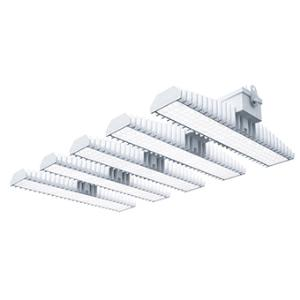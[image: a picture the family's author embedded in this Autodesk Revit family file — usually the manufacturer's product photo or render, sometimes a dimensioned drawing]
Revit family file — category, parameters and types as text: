
# Revit family: 3f_filippi_-_3f_lem_ho_ampio_3f_filippi_-_58976_a0812_-_3f_lem_5_ho_led_350_dali_cr_ampio___vs_a41a
name_source: partatom
category: Lighting Fixtures
units: mm (PartAtom-declared; Revit-internal decimal feet)

## family parameters
Cut with Voids When Loaded = No
Host = Face
Light Source = No
Part Type = Normal
Room Calculation Point = No
Round Connector Dimension = Use Diameter
Shared = No

## types (1)
- 3F Filippi - 3F LEM HO Ampio (1 x LED, 44256 lm, 345 W, 4000 K)
    Apparent Load = 345 VA
    Approval mark = CE
    CIE Flux Codes = 67 90 97 100 100
    Color Rendering = 80
    Color Temperature = 4000 K
    Control Gear = Electronic transformer
    Default Elevation = 1800 mm
    Description = Industrial luminaire with high light output and high luminous efficiency designed with the most innovative technologies for environments with temperature up to 55°C.

ILLUMINOTECHNICAL
Luminous efficiency 100% (DLOR 98%, ULOR 2%).
Initial luminous flux of the luminaire 44256 lm.
Direct symmetric wide distribution: the illuminated area has a rectangular shape.
Installation Interdistance Transv.D = 1.24 x hu - Long.D = 1.20 x hu.
Tabular UGR (CIE 117 - 4H-8H; S=0.25H; 70/50/20): RUG 23.8 - 23.9.
Beam angle: 82° - 83°.
Luminous efficacy 128 lm/W.
Lifetime (L93/B10): 30000 h. (tq+25°C)
Lifetime (L90/B10): 50000 h. (tq+25°C)
Lifetime (L85/B10): 80000 h. (tq+25°C)
Lifetime (L80/B10): 100000 h. (tq+25°C)
Lifetime (L85/B10): 50000 h. (tq+55°C)
Sudden decreased luminous flux after 50000 hours: 0% (C0).
Photobiological safety in compliance with IEC/TR 62778: RG0 risk exempt, (IEC 62471).
In compliance with IEC/EN 62722-2-1 - IEC/EN 62717 standards.

SOURCE
5 Mid-Power linear LED modules 70W/840.
Energy efficiency class (UE 2019/2020 - UE 2019/2015): C.
CIE 13.3 Colour rendering index: CRI >80 (R9 <50%).
IES TM-30 Fidelity Index: Rf = 84 Rg = 95.
CCT nominal colour temperature 4000 K.
Colour initial tolerance (MacAdam): SDCM 3.

MECHANICAL
Passive modular heatsinks in die-casted aluminium, painted in white colour.
To optimize the thermal management of the LED module, the heatsinks are oversized and provided with self-cleaning of cooling fins.
Wiring body in aluminium and galvanised steel anchored solidly to the sinks and thermally separated.
3F Lens lenses with high luminous efficiency, transparent methacrylate (PMMA), fixed to the LED modules.
Fixing brackets in stainless steel.
Luminaire with limited surface temperature. - D - (EN 60598-2-24)
Dimensions: 952x542 mm, height 133 mm. Weight 24.13 kg.
IP65 protection degree.
Mechanical strength to impacts IK06 (1 joule).
Glow-wire test resistance 650°C.

ELECTRICAL
Halogen Free DALI-2 DATI (Parts 251, 252, 253), PUSH-DIM, electronic wiring 230V-50/60Hz, power factor 0.97 at full load, THD <25%, constant output current, class I, 3 driver, 3 DALI addresses.
Power of the luminaire 345 W.
ENEC - CE.
SAFE FLICKER: PstLM=<1 and SVM=<0.4 (IEC TR 61547-1 and IEC TR 63158), to ensure a more comfortable and safe light.
Luminaire compliant with EN 60598-2-22 for power supply from a centralised emergency system CPSS (Central Power Supply System), not incorporated in the luminaire - high risk areas excluded. The default power and flux are 100% in AC and 15% in DC.
Ambient temperature from -30°C to +55°C.
Temperature class T6 max 85°C.
Quick connection via M25 5P connector with 9-13 mm tightening range.
Power unit positioned on a separate compartment by the LED module to ensure optimum temperatures of cabling components, to be inspectable and maintainable.
Relative humidity UR: <85%.

INSTALLATION
Ceiling / Suspended / Wall.
All accessories dedicated to this product are available on the Catalog and on our website www.3F-Filippi.com.

ACCESSORIES
A0812 - Anti-glare microprismatic VS moulded glass, tempered, not flammable, with sealing gasket.
One required for each light module. The pack contains 10 pieces.

APPLICATIONS
In commercial environments, exhibition and industrial areas, stores, open areas.
Environments in which it is necessary a total protection against falling fragments (eg environments with foodstuffs or machines with moving parts or with extreme temperature changes), use luminaires with polycarbonate lenses.

LIGHT MANAGEMENT
Recommended minimum setting: 10%.
The luminaire, equipped with (DALI-2 DATI) driver, can be controlled manually with 3F Easy Dim technology or automatically/manually with wired or wireless DALI/D2D control systems.
The D2D driver guarantees interoperability with other devices with the same certification by making the following information available:
Device Data (Part 251), Energy Report (Part 252), Diagnosis & Maintenance (Part 253).
In electrical systems without a regulation system (manual or automatic) and DALI bus, a suitable jumper must be made on the DA-DA terminals of the appliance.

WARNING
Fixture not suitable for cold stores with an ambient temperature <0°C and/or relative humidity >85%.
Luminaire designed for disposal/recycling at end-of-life.
Replaceable (LED only) light source by a professional. Replaceable control gear by a professional.
    Height = 133 mm  [stored 0.436352 ft]
    Lamp = 1 x LED
    Lamp Light Flux = 44256 lm
    Lamp Power = 345 W
    Lamp count = 1
    Length = 952 mm
    Lifetime = 50000 h
    Luminous efficacy = 128 lm/W
    Manufacturer = 3F Filippi
    ModVariant = No
    Model = 3F Filippi - 58976+A0812 - 3F LEM 5 HO LED 350 DALI CR AMPIO + VS
    Mounting Place = Ceiling
    Mounting Type = Pendant
    Number of Poles = 1
    OnlyDefault = Yes
    Power Factor = 1
    Product Name = 3F Filippi - 3F LEM HO Ampio
    Product group = pendant luminaire
    ProductGroupID = 9
    Protection Class = Protection class I
    Protection Degree = IP 65
    RLX_Detail_Level = 1
    RLX_Emergency_Light_Flux = 0 lm
    RLX_Emergency_Type = 0
    RLX_Emergency_Type_DB = No
    RlxData = <blob elided: 132161 chars, md5=47a88a7a>
    Socket = socket
    Standby Power = 0 W
    System Light Flux = 44256 lm
    System Power = 345 W
    Type Comments = Product without accessories
    Type Image = 3f_filippi_-_lem_5__a0812.jpg
    URL = http://relux.com
    VarID = ---
    Voltage = 0 V
    Weight = 0.00 kg
    Width = 542 mm

note: [stored X ft] marks values corroborated as IEEE doubles in the binary element streams (Revit-internal decimal feet)

## geometry (parser evidence)
native form markers: Blend x4, Sweep x12
no freeform markers — native parametric forms only
